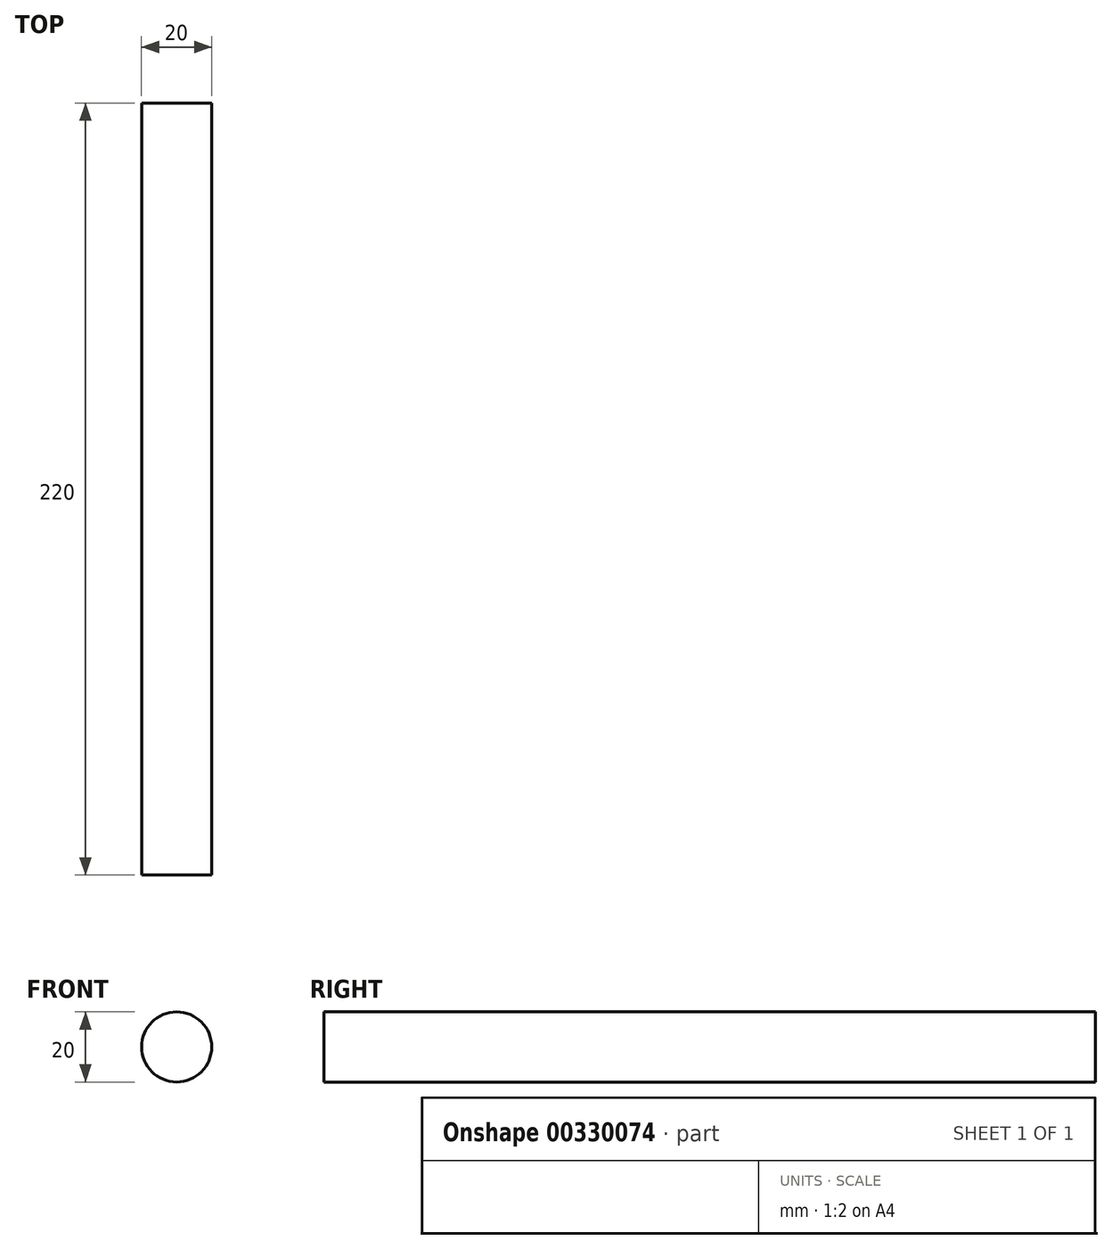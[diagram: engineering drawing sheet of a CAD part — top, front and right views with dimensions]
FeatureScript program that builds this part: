
annotation { "Feature Type Name" : "Feature", "Feature Type Description" : "" }
export const myFeature = defineFeature(function(context is Context, id is Id, definition is map)
    precondition{}
    {
        {
            var Q0;
            Q0=qCreatedBy(makeId("Front.planeOp"),FACE);
            var sketch = newSketch(context, id + "F0", { "sketchPlane" : qUnion([Q0])});
            skCircle(sketch, "E0", {"center": v(-59.45, 36.93) * mm, "radius": 10 * mm});
            skSolve(sketch);
        }
        {
            var Q0;
            Q0 = qSketchRegion(id + "F0", true);
            extrude(context, id + "F1", {"entities" : qUnion([Q0]), "depth" : 220 * mm, "offsetDistance" : 25 * mm});
        }
    });
